# Revit family: AQB
name_source: partatom
category: Mechanical Equipment
units: mm (PartAtom-declared; Revit-internal decimal feet)

## family parameters
Always vertical = Yes
Cut with Voids When Loaded = No
Part Type = Normal
Room Calculation Point = No
Round Connector Dimension = Use Diameter
Shared = No
Work Plane-Based = No

## types (5) — shared parameters
-(C/2) = -0' - 1 1/2"
0 = 0' - 0"
1" = 0' - 1"
1.5 = 0' - 1 1/2"
2" = 0' - 2"
2' = 2' - 0"
4" = 0' - 4"
BASE = 0' - 3"
BASE-.125 = 0' - 2 7/8"
Manufacturer = Loren Cook Company
Model = AQB
ONE EIGTH = 0' - 0 1/8"
Type Comments = Downblast Propeller Exhaust Ventilator Roof Mounted/Belt Drive
URL = www.lorencook.com

## per-type parameters (varying)
| type | (T_SQ/2)-2" | -(A/2) | A | A-1.5" | A-B | A/2 | B | B-C | B-C/2 | B/2 | C_ | C_/2 | D/2-(A-B) | RO | RO/2 | T_SQ | T_SQ/2 | T_SQ/2+.125" |
| 24_AQB | 1' - 4" | -1' - 0 7/16" | 2' - 0 7/8" | 1' - 11 3/8" | 1' - 3 3/4" | 1' - 0 7/16" | 0' - 9 1/8" | 0' - 6 1/8" | 0' - 3 1/16" | 0' - 4 9/16" | 3' - 11 1/2" | 1' - 11 3/4" | 0' - 8" | 2' - 7 1/2" | 1' - 3 3/4" | 3' - 0" | 1' - 6" | 1' - 6 1/8" |
| 30_AQB | 1' - 7" | -1' - 1 1/8" | 2' - 2 1/4" | 2' - 0 3/4" | 1' - 5" | 1' - 1 1/8" | 0' - 9 1/4" | 0' - 6 1/4" | 0' - 3 1/8" | 0' - 4 5/8" | 4' - 4 1/2" | 2' - 2 1/4" | 0' - 9 1/4" | 3' - 1 1/2" | 1' - 6 3/4" | 3' - 6" | 1' - 9" | 1' - 9 1/8" |
| 36_AQB | 1' - 10" | -1' - 1 5/8" | 2' - 3 1/4" | 2' - 1 3/4" | 1' - 5 1/2" | 1' - 1 5/8" | 0' - 9 3/4" | 0' - 6 3/4" | 0' - 3 3/8" | 0' - 4 7/8" | 5' - 2 1/2" | 2' - 7 1/4" | 1' - 1 3/4" | 3' - 7 1/2" | 1' - 9 3/4" | 4' - 0" | 2' - 0" | 2' - 0 1/8" |
| 42_AQB | 2' - 1" | -1' - 4 3/8" | 2' - 8 3/4" | 2' - 7 1/4" | 1' - 10 1/2" | 1' - 4 3/8" | 0' - 10 1/4" | 0' - 7 1/4" | 0' - 3 5/8" | 0' - 5 1/8" | 6' - 2 1/2" | 3' - 1 1/4" | 1' - 2 3/4" | 4' - 1 1/2" | 2' - 0 3/4" | 4' - 6" | 2' - 3" | 2' - 3 1/8" |
| 48_AQB | 2' - 4" | -1' - 4 3/8" | 2' - 8 3/4" | 2' - 7 1/4" | 1' - 10 1/2" | 1' - 4 3/8" | 0' - 10 1/4" | 0' - 7 1/4" | 0' - 3 5/8" | 0' - 5 1/8" | 6' - 2 1/2" | 3' - 1 1/4" | 1' - 2 3/4" | 4' - 7 1/2" | 2' - 3 3/4" | 5' - 0" | 2' - 6" | 2' - 6 1/8" |

## geometry (parser evidence)
native form markers: Sweep x2
no freeform markers — native parametric forms only
